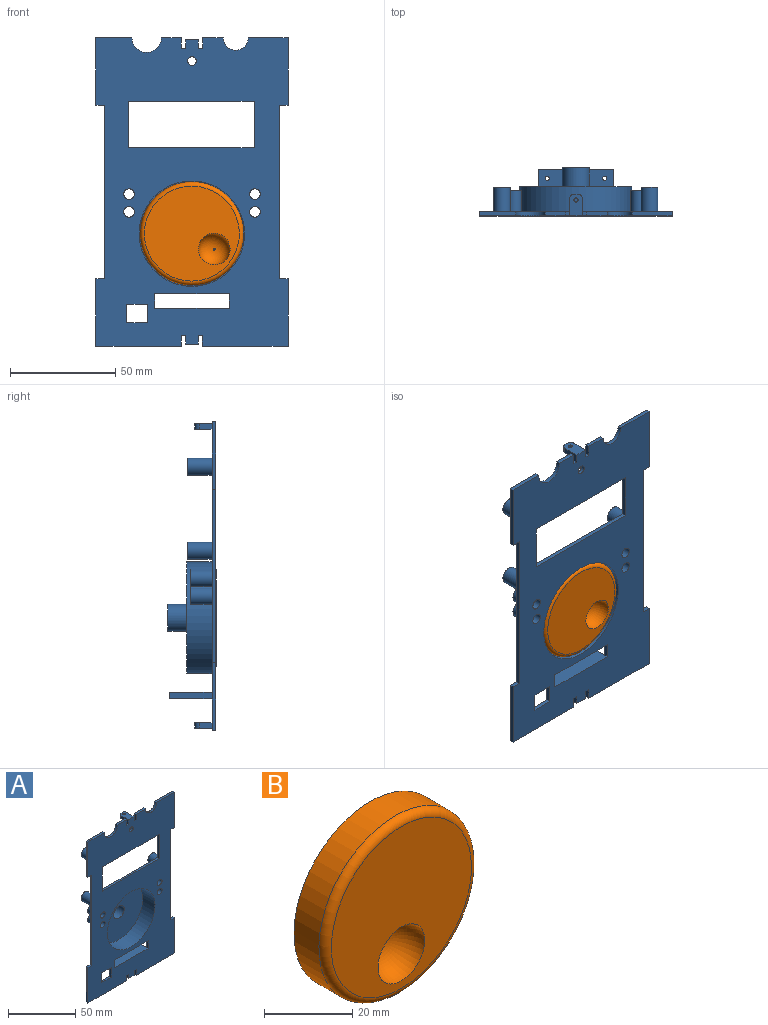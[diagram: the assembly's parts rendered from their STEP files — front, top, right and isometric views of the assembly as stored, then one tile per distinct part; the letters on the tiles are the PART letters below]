
ASSEMBLY  parts=2 mates=1
PART A: 100 faces, bbox 91.1x22.9x146.3 mm
  f0: plane 35.19x21.85mm, normal (0,0,1), area 762.7mm2, adj f4,f41,f45,f95,f96,f97,f98,f99
  f1: plane 35.19x20mm, normal (0,0,-1), area 697.6mm2, adj f2,f95,f96,f97,f98,f99
  f2: plane 146.29x91.14mm, normal (0,1,0), area 8074.3mm2, adj f1,f3,f4,f5,f6,f7,f8,f9
  f3: plane 35.19x1.85mm, normal (0,0,-1), area 65.1mm2, adj f2,f4,f41,f45
  f4: plane 7.01x1.85mm, normal (-1,0,0), area 13mm2, adj f0,f2,f3,f45
  f5: plane 17.1x1.85mm, normal (0,0,1), area 31.6mm2, adj f2,f6,f42,f45
  f6: plane 32.04x1.85mm, normal (-1,0,0), area 59.3mm2, adj f2,f5,f7,f45
  f7: plane 4.08x1.85mm, normal (0,0,-1), area 7.5mm2, adj f2,f6,f8,f45
  f8: plane 82.19x1.85mm, normal (-1,0,0), area 152.1mm2, adj f2,f7,f9,f45
  f9: plane 4.08x1.85mm, normal (0,0,1), area 7.5mm2, adj f2,f8,f10,f45
  f10: plane 32.05x1.85mm, normal (-1,0,0), area 59.3mm2, adj f2,f9,f11,f45
  f11: plane 40.55x1.85mm, normal (0,0,-1), area 75mm2, adj f2,f10,f12,f45
  f12: plane 5.03x1.85mm, normal (1,0,0), area 9.3mm2, adj f2,f11,f13,f45
  f13: plane 2x1.85mm, normal (0,0,-1), area 3.7mm2, adj f2,f12,f14,f45
  f14: plane 8x3.98mm, normal (-1,0,0), area 22.7mm2, adj f2,f13,f45,f49,f51,f53
  f15: plane 8x3.98mm, normal (1,0,0), area 22.7mm2, adj f2,f16,f45,f49,f51,f52
  f16: plane 2x1.85mm, normal (0,0,-1), area 3.7mm2, adj f2,f15,f17,f45
  f17: plane 5.03x1.85mm, normal (-1,0,0), area 9.3mm2, adj f2,f16,f18,f45
  f18: plane 40.59x1.85mm, normal (0,0,-1), area 75.1mm2, adj f2,f17,f19,f45
  f19: plane 32.05x1.85mm, normal (1,0,0), area 59.3mm2, adj f2,f18,f20,f45
  f20: plane 4.09x1.85mm, normal (0,0,1), area 7.6mm2, adj f2,f19,f21,f45
  f21: plane 82.19x1.85mm, normal (1,0,0), area 152.1mm2, adj f2,f20,f22,f45
  f22: plane 4.09x1.85mm, normal (0,0,-1), area 7.6mm2, adj f2,f21,f23,f45
  f23: plane 32.04x1.85mm, normal (1,0,0), area 59.3mm2, adj f2,f22,f24,f45
  f24: plane 18.9x1.85mm, normal (0,0,1), area 35mm2, adj f2,f23,f25,f45
  f25: cylinder r=5.92mm len=11.84mm, axis (0,1,0), area 34.4mm2, adj f2,f24,f26,f45
  f26: plane 9.84x1.85mm, normal (0,0,1), area 18.2mm2, adj f2,f25,f27,f45
  f27: plane 5x1.85mm, normal (-1,0,0), area 9.3mm2, adj f2,f26,f28,f45
  f28: plane 2x1.85mm, normal (0,0,1), area 3.7mm2, adj f2,f27,f29,f45
  f29: plane 8x3.99mm, normal (1,0,0), area 22.8mm2, adj f2,f28,f45,f46,f48,f54
  f30: plane 8x3.99mm, normal (-1,0,0), area 22.8mm2, adj f2,f31,f45,f46,f48,f55
  f31: plane 1.98x1.85mm, normal (0,0,1), area 3.7mm2, adj f2,f30,f32,f45
  f32: plane 5x1.85mm, normal (1,0,0), area 9.3mm2, adj f2,f31,f33,f45
  f33: plane 9.48x1.85mm, normal (0,0,1), area 17.5mm2, adj f2,f32,f42,f45
  f34: plane 8.73x1.85mm, normal (1,0,0), area 16.2mm2, adj f2,f35,f43,f45
  f35: plane 9.87x1.85mm, normal (0,0,-1), area 18.3mm2, adj f2,f34,f36,f45
  f36: plane 8.73x1.85mm, normal (-1,0,0), area 16.2mm2, adj f2,f35,f43,f45
  f37: plane 22.05x1.85mm, normal (1,0,0), area 40.8mm2, adj f2,f38,f44,f45
  f38: plane 59.69x1.85mm, normal (0,0,-1), area 110.4mm2, adj f2,f37,f39,f45
  f39: plane 22.05x1.85mm, normal (-1,0,0), area 40.8mm2, adj f2,f38,f44,f45
  f40: cylinder r=2.05mm len=4.11mm, axis (0,1,0), area 23.9mm2, adj f2,f45
  f41: plane 7.01x1.85mm, normal (1,0,0), area 13mm2, adj f0,f2,f3,f45
  f42: cylinder r=7mm len=14mm, axis (0,1,0), area 40.7mm2, adj f2,f5,f33,f45
  f43: plane 9.87x1.85mm, normal (0,0,1), area 18.3mm2, adj f2,f34,f36,f45
  f44: plane 59.69x1.85mm, normal (0,0,1), area 110.4mm2, adj f2,f37,f39,f45
  f45: plane 146.29x91.14mm, normal (0,-1,0), area 8772.4mm2, adj f0,f3,f4,f5,f6,f7,f8,f9
  f46: plane 8.15x5.99mm, normal (0,0,-1), area 44mm2, adj f2,f29,f30,f47,f54,f55,f57
  f47: plane 2.5x1.99mm, normal (0,1,0), area 5mm2, adj f46,f48,f54,f55
  f48: plane 10x5.99mm, normal (0,0,1), area 55.1mm2, adj f29,f30,f45,f47,f54,f55,f57
  f49: plane 8.15x5.99mm, normal (0,0,1), area 44mm2, adj f2,f14,f15,f50,f52,f53,f56
  f50: plane 2.5x1.99mm, normal (0,1,0), area 5mm2, adj f49,f51,f52,f53
  f51: plane 10x5.99mm, normal (0,0,-1), area 55.1mm2, adj f14,f15,f45,f50,f52,f53,f56
  f52: cylinder r=2mm len=2.5mm, axis (0,0,-1), area 7.9mm2, adj f15,f49,f50,f51
  f53: cylinder r=2mm len=2.5mm, axis (0,0,1), area 7.9mm2, adj f14,f49,f50,f51
  f54: cylinder r=2mm len=2.5mm, axis (0,0,-1), area 7.9mm2, adj f29,f46,f47,f48
  f55: cylinder r=2mm len=2.5mm, axis (0,0,1), area 7.9mm2, adj f30,f46,f47,f48
  f56: cylinder r=1mm len=2.5mm, axis (0,0,1), area 15.7mm2, adj f49,f51
  f57: cylinder r=1mm len=2.5mm, axis (0,0,1), area 15.7mm2, adj f46,f48
  f58: cylinder r=2mm len=11.5mm, axis (0,-1,0), area 144.5mm2, adj f60,f61
  f59: cylinder r=4mm len=11.5mm, axis (0,-1,0), area 289mm2, adj f2,f60
  f60: plane 8x8mm, normal (0,1,0), area 37.7mm2, adj f58,f59
  f61: plane 4x4mm, normal (0,1,0), area 12.6mm2, adj f58
  f62: cylinder r=2mm len=11.5mm, axis (0,-1,0), area 144.5mm2, adj f64,f65
  f63: cylinder r=4mm len=11.5mm, axis (0,-1,0), area 289mm2, adj f2,f64
  f64: plane 8x8mm, normal (0,1,0), area 37.7mm2, adj f62,f63
  f65: plane 4x4mm, normal (0,1,0), area 12.6mm2, adj f62
  f66: cylinder r=2mm len=11.5mm, axis (0,-1,0), area 144.5mm2, adj f68,f69
  f67: cylinder r=4mm len=11.5mm, axis (0,-1,0), area 289mm2, adj f2,f68
  f68: plane 8x8mm, normal (0,1,0), area 37.7mm2, adj f66,f67
  f69: plane 4x4mm, normal (0,1,0), area 12.6mm2, adj f66
  f70: cylinder r=2mm len=11.5mm, axis (0,-1,0), area 144.5mm2, adj f72,f73
  f71: cylinder r=4mm len=11.5mm, axis (0,-1,0), area 289mm2, adj f2,f72
  f72: plane 8x8mm, normal (0,1,0), area 37.7mm2, adj f70,f71
  f73: plane 4x4mm, normal (0,1,0), area 12.6mm2, adj f70
  f74: cylinder r=4mm len=10mm, axis (0,1,0), area 251.3mm2, adj f2,f76
  f75: cylinder r=2.5mm len=11.85mm, axis (0,1,0), area 186.1mm2, adj f45,f76
  f76: plane 8x8mm, normal (0,1,0), area 30.6mm2, adj f74,f75
  f77: cylinder r=4mm len=10mm, axis (0,1,0), area 251.3mm2, adj f2,f79
  f78: cylinder r=2.5mm len=11.85mm, axis (0,1,0), area 186.1mm2, adj f45,f79
  f79: plane 8x8mm, normal (0,1,0), area 30.6mm2, adj f77,f78
  f80: cylinder r=4mm len=10mm, axis (0,1,0), area 251.3mm2, adj f2,f82
  f81: cylinder r=2.5mm len=11.85mm, axis (0,1,0), area 186.1mm2, adj f45,f82
  f82: plane 8x8mm, normal (0,1,0), area 30.6mm2, adj f80,f81
  f83: cylinder r=4mm len=10mm, axis (0,1,0), area 251.3mm2, adj f2,f85
  f84: cylinder r=2.5mm len=11.85mm, axis (0,1,0), area 186.1mm2, adj f45,f85
  f85: plane 8x8mm, normal (0,1,0), area 30.6mm2, adj f83,f84
  f86: cylinder r=26.5mm len=53mm, axis (0,1,0), area 1998.1mm2, adj f2,f88
  f87: cylinder r=25mm len=50mm, axis (0,1,0), area 2018.5mm2, adj f45,f89
  f88: plane 53x53mm, normal (0,1,0), area 2077.5mm2, adj f86,f90
  f89: plane 50x50mm, normal (0,-1,0), area 1868.5mm2, adj f87,f92
  f90: cylinder r=6.4mm len=12.8mm, axis (0,-1,0), area 361.9mm2, adj f88,f91
  f91: plane 12.8x12.8mm, normal (0,1,0), area 90.2mm2, adj f90,f94
  f92: cylinder r=5.5mm len=11mm, axis (0,-1,0), area 276.5mm2, adj f89,f93
  f93: plane 11x11mm, normal (0,-1,0), area 56.5mm2, adj f92,f94
  f94: cylinder r=3.5mm len=7mm, axis (0,-1,0), area 44mm2, adj f91,f93
  f95: plane 20x2.89mm, normal (1,0,0), area 57.9mm2, adj f0,f1,f2,f97
  f96: plane 20x2.89mm, normal (-1,0,0), area 57.9mm2, adj f0,f1,f2,f97
  f97: plane 35.19x2.89mm, normal (0,1,0), area 101.9mm2, adj f0,f1,f95,f96
  f98: cylinder r=1mm len=2.89mm, axis (0,0,-1), area 18.2mm2, adj f0,f1
  f99: cylinder r=1mm len=2.89mm, axis (0,0,-1), area 18.2mm2, adj f0,f1
PART B: 9 faces, bbox 53x10x53 mm
  f0: cylinder r=24.5mm len=49mm, axis (0,1,0), area 1231.5mm2, adj f2,f3
  f1: plane 45x45mm, normal (0,-1,0), area 1413.7mm2, adj f3,f8
  f2: plane 49x49mm, normal (0,1,0), area 1861mm2, adj f0,f4,f5
  f3: torus R=22.5mm, axis (0,-1,0), area 469.3mm2, adj f0,f1
  f4: plane 9x5.4mm, normal (1,0,0), area 48.6mm2, adj f2,f5,f6
  f5: cylinder r=3.12mm len=9mm, axis (0,1,0), area 118.1mm2, adj f2,f4,f6
  f6: plane 6.25x4.7mm, normal (0,1,0), area 24.7mm2, adj f4,f5
  f7: plane 1x1mm, normal (0,-1,0), area 0.8mm2, adj f8
  f8: torus R=0.5mm, axis (0,-1,0), area 342.4mm2, adj f1,f7
PLACE A t=(-50.85,22.82,31.57)mm fixed
PLACE B rot(axis=(0,-1,0),55.4deg) t=(-50.92,30.82,11.83)mm
MATE revolute B.f0 <-> A.f86  axis (0,1,0) through (-50.92,30.82,11.82)mm
